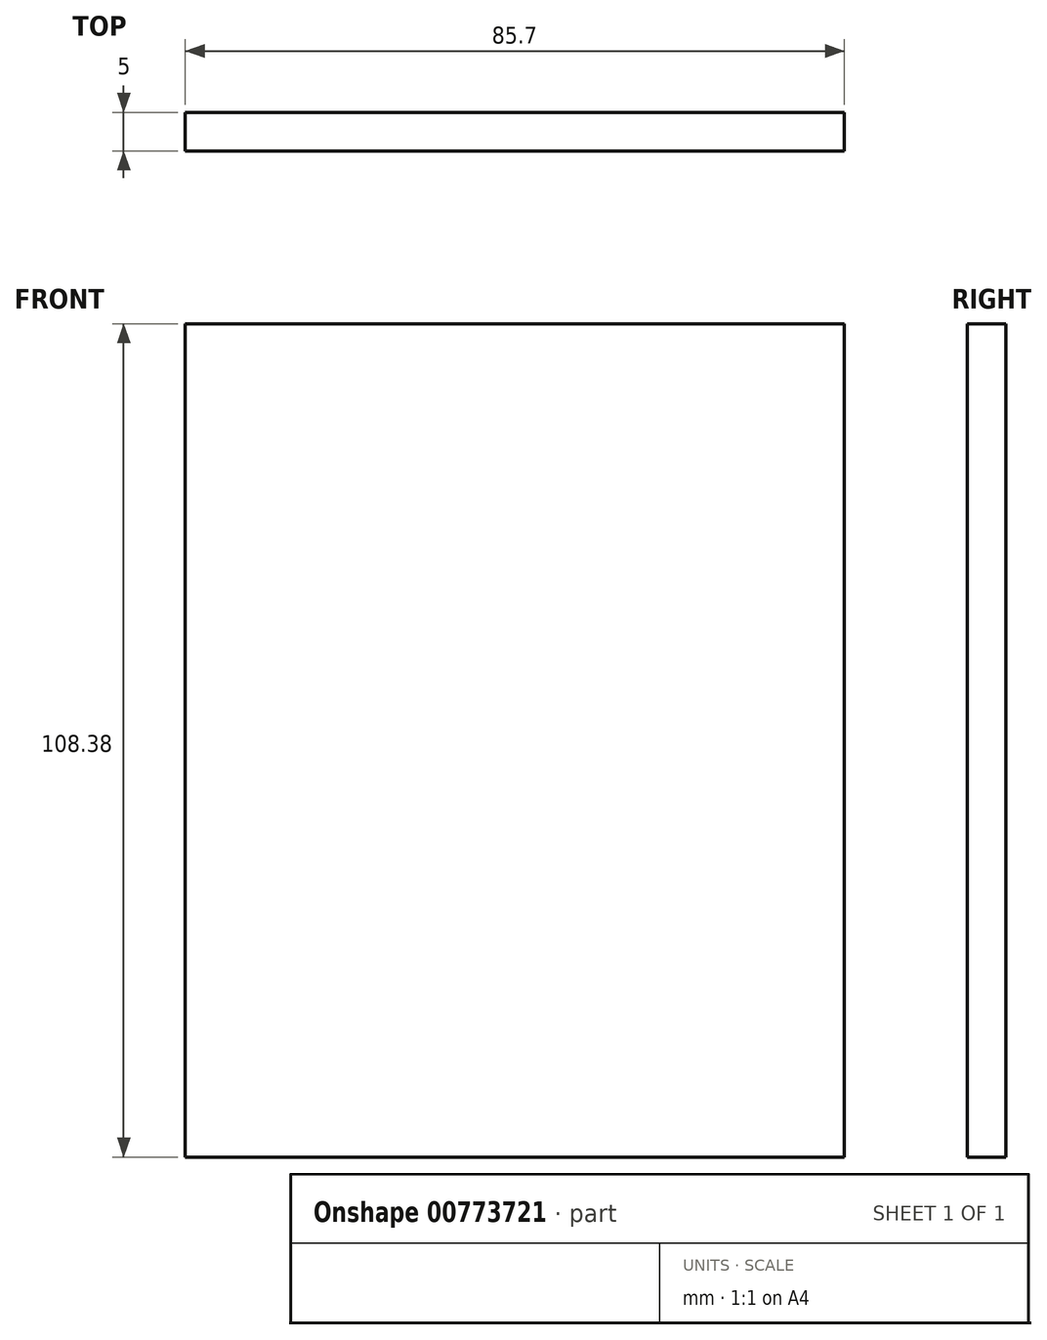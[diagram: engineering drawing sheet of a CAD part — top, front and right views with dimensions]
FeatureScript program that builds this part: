
annotation { "Feature Type Name" : "Feature", "Feature Type Description" : "" }
export const myFeature = defineFeature(function(context is Context, id is Id, definition is map)
    precondition{}
    {
        {
            var Q0;
            Q0=qCreatedBy(makeId("Front.planeOp"),FACE);
            var sketch = newSketch(context, id + "F0", { "sketchPlane" : qUnion([Q0])});
            skLineSegment(sketch, "E0.bottom", {"start": v(42.85, -42.95) * mm, "end": v(-42.85, -42.95) * mm});
            skLineSegment(sketch, "E0.top", {"start": v(42.85, 65.43) * mm, "end": v(-42.85, 65.43) * mm});
            skLineSegment(sketch, "E0.left", {"start": v(42.85, -42.95) * mm, "end": v(42.85, 65.43) * mm});
            skLineSegment(sketch, "E0.right", {"start": v(-42.85, -42.95) * mm, "end": v(-42.85, 65.43) * mm});
            skPoint(sketch, "E0.middle", {"position": v(0, 11.24) * mm});
            skSolve(sketch);
        }
        {
            var Q0;
            Q0=makeQuery(id+"F0.imprint","IMPRINT",FACE,{"disambiguationData":[TD([[makeQuery(id+"F0.imprint","IMPRINT",EDGE,{"derivedFrom":sQuery(id+"F0.wireOp",EDGE,"E0.bottom")}),-1.0]])]});
            extrude(context, id + "F1", {"entities" : qUnion([Q0]), "depth" : 5 * mm, "offsetDistance" : 25 * mm});
        }
    });
